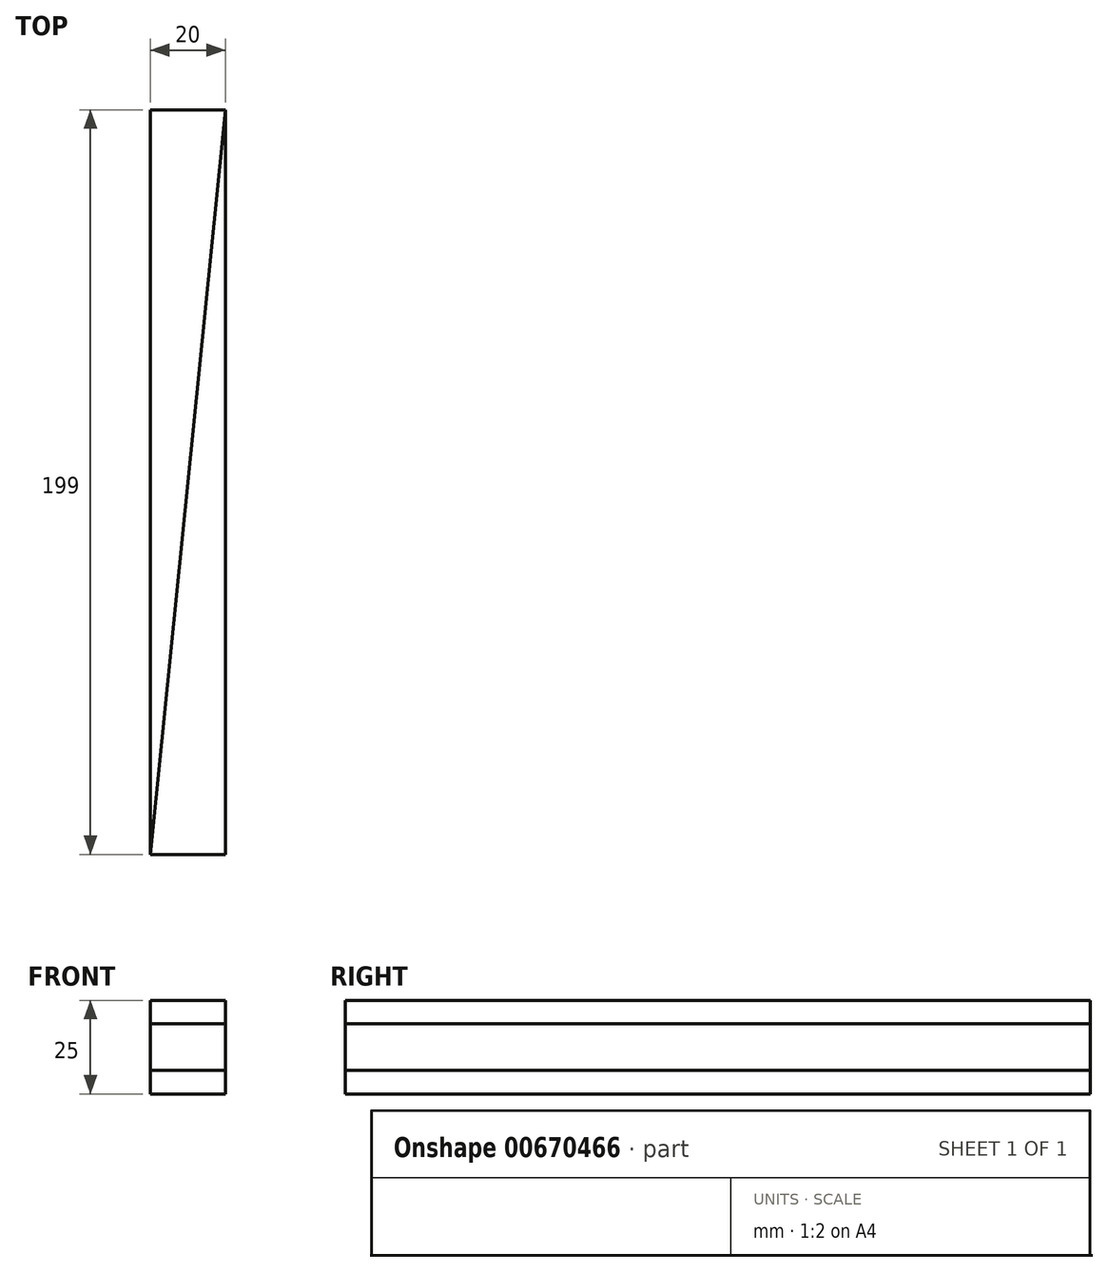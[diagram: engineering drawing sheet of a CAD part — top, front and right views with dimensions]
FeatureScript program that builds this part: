
annotation { "Feature Type Name" : "Feature", "Feature Type Description" : "" }
export const myFeature = defineFeature(function(context is Context, id is Id, definition is map)
    precondition{}
    {
        {
            var Q0;
            Q0=qCreatedBy(makeId("Top.planeOp"),FACE);
            var sketch = newSketch(context, id + "F0", { "sketchPlane" : qUnion([Q0])});
            skLineSegment(sketch, "E0.bottom", {"start": v(-10, -99.5) * mm, "end": v(10, -99.5) * mm});
            skLineSegment(sketch, "E0.top", {"start": v(-10, 99.5) * mm, "end": v(10, 99.5) * mm});
            skLineSegment(sketch, "E0.left", {"start": v(-10, -99.5) * mm, "end": v(-10, 99.5) * mm});
            skLineSegment(sketch, "E0.right", {"start": v(10, -99.5) * mm, "end": v(10, 99.5) * mm});
            skPoint(sketch, "E0.middle", {"position": v(0, 0) * mm});
            skLineSegment(sketch, "E1", {"start": v(-10, -99.5) * mm, "end": v(10, 99.5) * mm});
            skSolve(sketch);
        }
        {
            var Q0;
            Q0=makeQuery(id+"F0.imprint","IMPRINT",FACE,{"disambiguationData":[TD([[makeQuery(id+"F0.imprint","IMPRINT",EDGE,{"derivedFrom":sQuery(id+"F0.wireOp",EDGE,"E0.top")}),-1.0]])]});
            extrude(context, id + "F1", {"entities" : qUnion([Q0]), "endBound" : BoundingType.SYMMETRIC, "depth" : 25 * mm, "offsetDistance" : 25 * mm});
        }
        {
            var Q0;
            Q0=makeQuery(id+"F0.imprint","IMPRINT",FACE,{"disambiguationData":[TD([[makeQuery(id+"F0.imprint","IMPRINT",EDGE,{"derivedFrom":sQuery(id+"F0.wireOp",EDGE,"E0.bottom")}),1.0]])]});
            extrude(context, id + "F2", {"entities" : qUnion([Q0]), "endBound" : BoundingType.SYMMETRIC, "depth" : 12.5 * mm, "offsetDistance" : 25 * mm});
        }
    });
